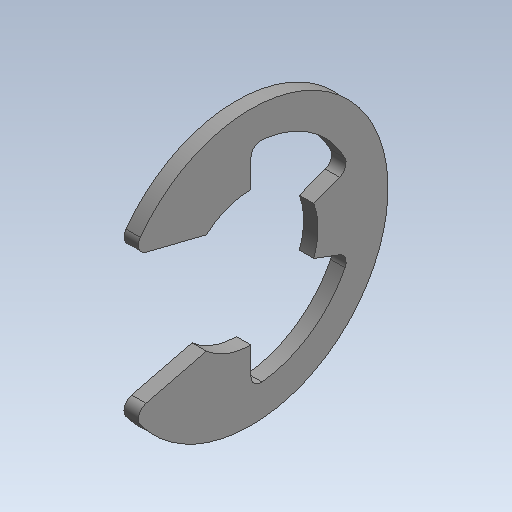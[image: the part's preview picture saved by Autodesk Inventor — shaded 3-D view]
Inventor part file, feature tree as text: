
AUTODESK INVENTOR PART (.ipt)
format: ipt  version: 2020 (Build 240168000, 168)  size: 101,888 bytes
history: native  units: mm (DEFAULTED — no unit token found)
features: fillet x1
ambient origin geometry x8: Origin, YZ Plane, XZ Plane, XY Plane, X Axis, Y Axis, Z Axis, Center Point
bodies: Solid1 (feature_tree)
feature tree (1):
  fillet  "Fillet1"  [1 undecoded]
note: 1 required parameter value undecoded (feature->parameter linkage not recoverable at this tier; creation-order binding heuristic only, values carry confidence <= 0.55)
